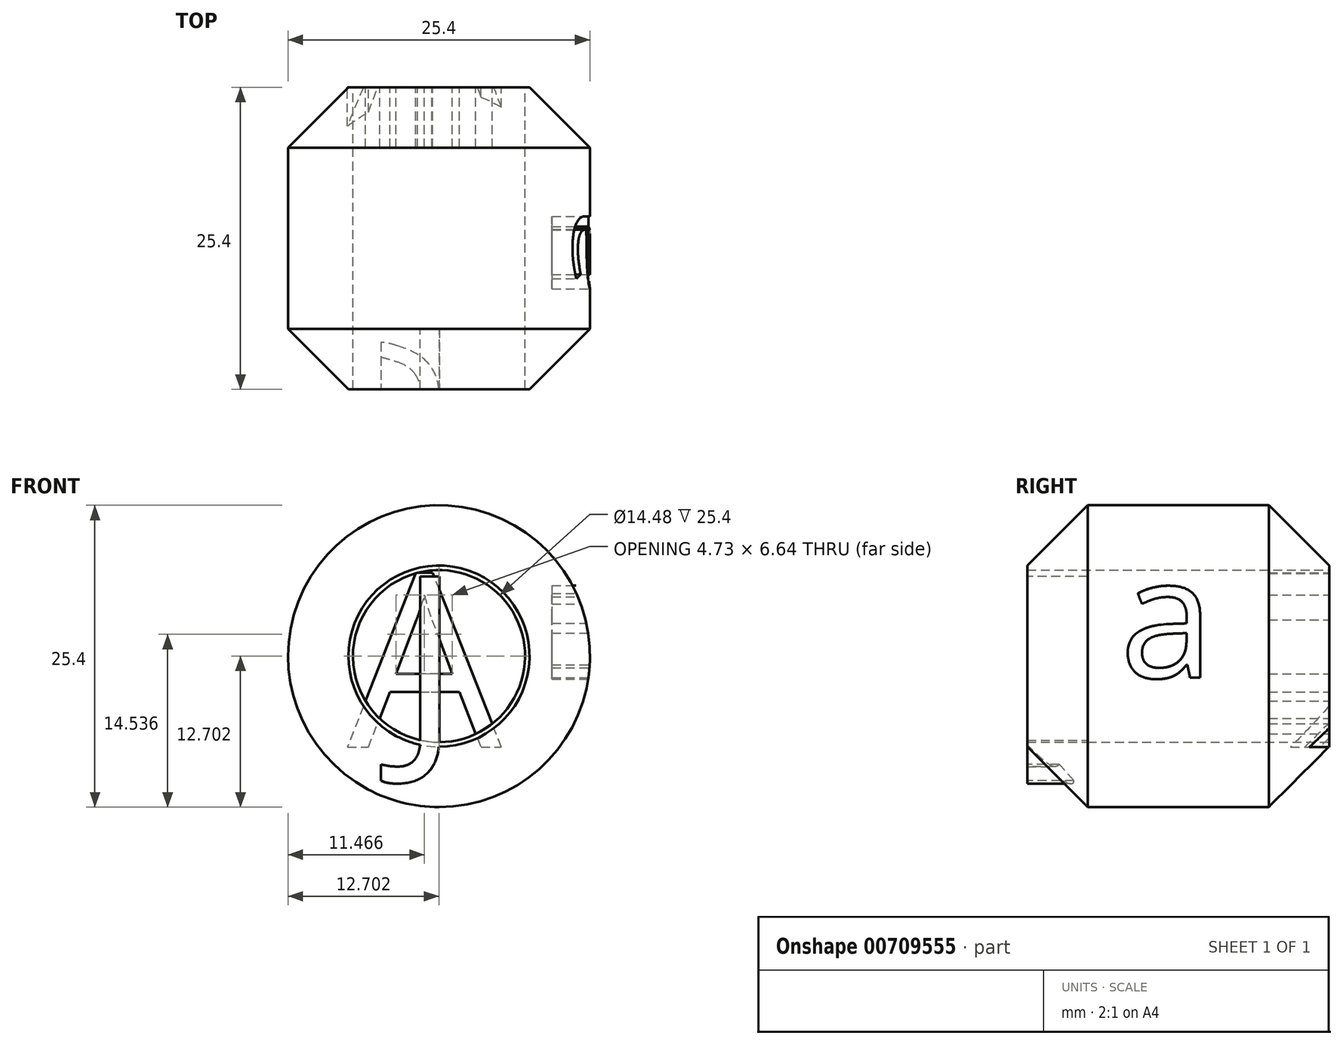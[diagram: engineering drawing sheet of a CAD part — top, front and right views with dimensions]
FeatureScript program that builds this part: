
annotation { "Feature Type Name" : "Feature", "Feature Type Description" : "" }
export const myFeature = defineFeature(function(context is Context, id is Id, definition is map)
    precondition{}
    {
        {
            var Q0;
            Q0=qCreatedBy(makeId("Front.planeOp"),FACE);
            var sketch = newSketch(context, id + "F0", { "sketchPlane" : qUnion([Q0])});
            skCircle(sketch, "E0", {"center": v(-14.59, 27.52) * mm, "radius": 12.7 * mm});
            skSolve(sketch);
        }
        {
            var Q0;
            Q0=makeQuery(id+"F0.imprint","IMPRINT",FACE,{"disambiguationData":[TD([[makeQuery(id+"F0.imprint","IMPRINT",EDGE,{"derivedFrom":sQuery(id+"F0.wireOp",EDGE,"E0")}),1.0]])]});
            extrude(context, id + "F1", {"entities" : qUnion([Q0]), "depth" : 25.4 * mm, "offsetDistance" : 25.4 * mm});
        }
        {
            var Q0;
            Q0=makeQuery(id+"F1.opExtrude","CAP_FACE",FACE,{"disambiguationData":[OSD([sQuery(id+"F0.wireOp",EDGE,"E0")])],"isStart":false});
            var Q1;
            Q1=makeQuery(id+"F1.opExtrude","CAP_EDGE",EDGE,{"disambiguationData":[OSD([sQuery(id+"F0.wireOp",EDGE,"E0")])],"isStart":true});
            chamfer(context, id + "F2", {"entities" : qUnion([Q0, Q1]), "width" : 5.08 * mm, "tangentPropagation" : true});
        }
        {
            var Q0;
            Q0=makeQuery(id+"F1.opExtrude","CAP_FACE",FACE,{"disambiguationData":[OSD([sQuery(id+"F0.wireOp",EDGE,"E0")])],"isStart":true});
            var sketch = newSketch(context, id + "F3", { "sketchPlane" : qUnion([Q0])});
            skCircle(sketch, "E1", {"center": v(14.59, 27.52) * mm, "radius": 7.24 * mm});
            skSolve(sketch);
        }
        {
            var Q0;
            Q0 = qSketchRegion(id + "F3", true);
            extrude(context, id + "F4", {"entities" : qUnion([Q0]), "operationType" : NewBodyOperationType.REMOVE, "endBound" : BoundingType.THROUGH_ALL, "oppositeDirection" : true, "depth" : 25.4 * mm, "offsetDistance" : 25.4 * mm});
        }
        {
            var Q0;
            Q0=qCreatedBy(makeId("Right.planeOp"),FACE);
            var sketch = newSketch(context, id + "F5", { "sketchPlane" : qUnion([Q0])});
            skText(sketch, "E2", { "text": "a", "fontName": "OpenSans-Regular.ttf"});
            const initialGuessF5  = {"E2": [-0.0176, 0.02572, 1, 0, 0.01023]};
            skSetInitialGuess(sketch, initialGuessF5);
            skSolve(sketch);
        }
        {
            var Q0;
            Q0 = qSketchRegion(id + "F5", true);
            extrude(context, id + "F6", {"entities" : qUnion([Q0]), "operationType" : NewBodyOperationType.REMOVE, "oppositeDirection" : true, "depth" : 5.08 * mm, "offsetDistance" : 25.4 * mm});
        }
        {
            var Q0;
            Q0=makeQuery(id+"F1.opExtrude","CAP_FACE",FACE,{"disambiguationData":[OSD([sQuery(id+"F0.wireOp",EDGE,"E0")])],"isStart":false});
            var sketch = newSketch(context, id + "F7", { "sketchPlane" : qUnion([Q0])});
            skText(sketch, "E3", { "text": "J", "fontName": "OpenSans-Regular.ttf"});
            const initialGuessF7  = {"E3": [-0.01796, 0.02043, 1, 0, 0.01392]};
            skSetInitialGuess(sketch, initialGuessF7);
            skSolve(sketch);
        }
        {
            var Q0;
            Q0 = qSketchRegion(id + "F7", true);
            extrude(context, id + "F8", {"entities" : qUnion([Q0]), "operationType" : NewBodyOperationType.ADD, "oppositeDirection" : true, "depth" : 5.08 * mm, "offsetDistance" : 25.4 * mm});
        }
        {
            var Q0;
            Q0=makeQuery(id+"F1.opExtrude","CAP_FACE",FACE,{"disambiguationData":[OSD([sQuery(id+"F0.wireOp",EDGE,"E0")])],"isStart":true});
            var sketch = newSketch(context, id + "F9", { "sketchPlane" : qUnion([Q0])});
            skText(sketch, "E4", { "text": "A", "fontName": "OpenSans-Regular.ttf"});
            const initialGuessF9  = {"E4": [0.00934, 0.01986, 1, 0, 0.01474]};
            skSetInitialGuess(sketch, initialGuessF9);
            skSolve(sketch);
        }
        {
            var Q0;
            Q0 = qSketchRegion(id + "F9", true);
            extrude(context, id + "F10", {"entities" : qUnion([Q0]), "operationType" : NewBodyOperationType.ADD, "oppositeDirection" : true, "depth" : 5.08 * mm, "offsetDistance" : 25.4 * mm});
        }
    });
